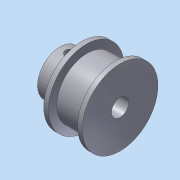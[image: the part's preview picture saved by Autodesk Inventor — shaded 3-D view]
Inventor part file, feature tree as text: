
AUTODESK INVENTOR PART (.ipt)
format: ipt  version: 2013 (Build 170138000, 138)  size: 138,752 bytes
history: native  units: mm
features: sketch x3, hole x2, revolve x1, plane x1, pattern_circular x1, projected_geometry x1
ambient origin geometry x8: Origin, YZ Plane, XZ Plane, XY Plane, X Axis, Y Axis, Z Axis, Center Point
bodies: Solid1 (feature_tree)
feature tree (9):
  revolve  "Revolution1"  [1 undecoded]
  hole  "Hole1"  [1 undecoded]
  plane  "Work Plane1"
  hole  "Hole2"  [1 undecoded]
  pattern_circular  "Circular Pattern1"  [2 undecoded]
  sketch  "Sketch1"  dims[d0=13.0mm d2=22.0mm]
  sketch  "Sketch2"  dims[d3=11.2mm d4=1.358mm]
  sketch  "Sketch4"  dims[d5=8.0mm d6=1.358mm d7=17.625mm d8=6.3mm d9=17.5mm d11=90.0deg d12=5.0mm d13=6.0mm d14=4.0mm d15=2.0mm d16=90.0deg d17=8.0mm d18=20.594885mm d19=3.0mm d20=6.0mm d21=4.0mm d22=2.0mm d23=90.0deg d24=8.0mm d25=20.594885mm d26=20.0mm d27=-15.707963mm]
  projected_geometry  "Projected Loop2"
note: 5 required parameter values undecoded (feature->parameter linkage not recoverable at this tier; creation-order binding heuristic only, values carry confidence <= 0.55)